# Revit family: Урна для раздельного сбора мусора «Опус» Арт 12765
name_source: partatom
category: Антураж
revit_build: Autodesk Revit 2018 (Build: 20180423_1000(x64)
units: mm (PartAtom-declared; Revit-internal decimal feet)

## family parameters
Всегда вертикально = Да
Источник визуального образа = Геометрия семейства
На основе рабочей плоскости = Нет
Общий = Нет
При загрузке вырезать с полостями = Нет
Точка расчета площади = Нет

## types (2) — shared parameters
URL = https://hobbyka.ru
Артикул товара = Арт. 12765
Высота = 900 мм
Группа модели = Уличные урны
Изготовитель = ООО «Хоббика»
Комментарий по цветам = Цвет отходов 1-1 - для одинарной модели. Цвет отходов 4-1 - 4-4 - для четырехсекционной модели
Материал изделия = Сталь
Цвет каркаса = Сталь
Цвет опоры = Опора
Цвет отходов 1-1 = Тип отходов
Ширина = 400 мм

## per-type parameters (varying)
| type | 1 секция | 4 секции | Длина | Изображение типоразмера | Цвет отходов 4-1 | Цвет отходов 4-2 | Цвет отходов 4-3 | Цвет отходов 4-4 |
| Урна для раздельного сбора мусора «Опус». Одинарная | Да | Нет | 400 мм | Урна для раздельного сбора мусора «Опус» Арт 12765 1 секция.jpg | Тип отходов | Тип отходов | Тип отходов | Тип отходов |
| Урна для раздельного сбора мусора «Опус». Четырехсекционная | Нет | Да | 1600 мм | Урна для раздельного сбора мусора «Опус» Арт 12765 4 секции.jpg | Отходы пластик | Отходы бумага | Отходы металл | Отходы несортируемые |

note: column(s) folded — value = type name in every type: Описание
